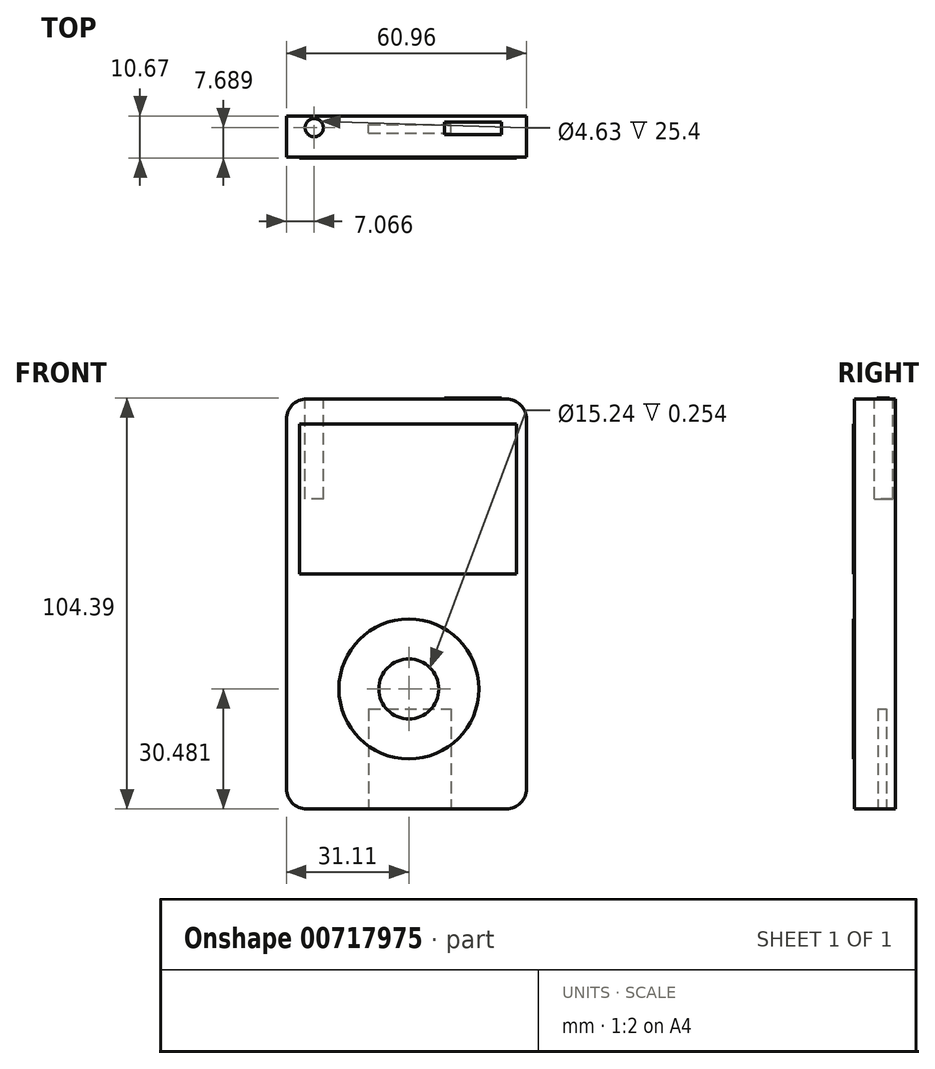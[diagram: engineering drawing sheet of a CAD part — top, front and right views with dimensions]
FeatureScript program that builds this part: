
annotation { "Feature Type Name" : "Feature", "Feature Type Description" : "" }
export const myFeature = defineFeature(function(context is Context, id is Id, definition is map)
    precondition{}
    {
        {
            var Q0;
            Q0=qCreatedBy(makeId("Front.planeOp"),FACE);
            var sketch = newSketch(context, id + "F0", { "sketchPlane" : qUnion([Q0])});
            skLineSegment(sketch, "E0.bottom", {"start": v(22.89, -46.83) * mm, "end": v(-38.07, -46.83) * mm});
            skLineSegment(sketch, "E0.top", {"start": v(22.89, 57.31) * mm, "end": v(-38.07, 57.31) * mm});
            skLineSegment(sketch, "E0.left", {"start": v(22.89, -46.83) * mm, "end": v(22.89, 57.31) * mm});
            skLineSegment(sketch, "E0.right", {"start": v(-38.07, -46.83) * mm, "end": v(-38.07, 57.31) * mm});
            skSolve(sketch);
        }
        {
            var Q0;
            Q0 = qSketchRegion(id + "F0", true);
            extrude(context, id + "F1", {"entities" : qUnion([Q0]), "depth" : 10.4 * mm, "offsetDistance" : 25.4 * mm});
        }
        {
            var Q0;
            Q0=makeQuery(id+"F1.opExtrude","CAP_FACE",FACE,{"disambiguationData":[OSD([sQuery(id+"F0.wireOp",EDGE,"E0.bottom"),sQuery(id+"F0.wireOp",EDGE,"E0.top"),sQuery(id+"F0.wireOp",EDGE,"E0.left"),sQuery(id+"F0.wireOp",EDGE,"E0.right")])],"isStart":false});
            var sketch = newSketch(context, id + "F2", { "sketchPlane" : qUnion([Q0])});
            skLineSegment(sketch, "E1.bottom", {"start": v(-34.8, 50.96) * mm, "end": v(20.39, 50.96) * mm});
            skLineSegment(sketch, "E1.top", {"start": v(-34.8, 12.86) * mm, "end": v(20.39, 12.86) * mm});
            skLineSegment(sketch, "E1.left", {"start": v(-34.8, 50.96) * mm, "end": v(-34.8, 12.86) * mm});
            skLineSegment(sketch, "E1.right", {"start": v(20.39, 50.96) * mm, "end": v(20.39, 12.86) * mm});
            skLineSegment(sketch, "E2", {"start": v(-38.07, 57.31) * mm, "end": v(-38.07, 31.91) * mm});
            skPoint(sketch, "E2.endSnap0", {"position": v(-34.8, 31.91) * mm});
            skSolve(sketch);
        }
        {
            var Q0;
            Q0=makeQuery(id+"F2.imprint","IMPRINT",FACE,{"disambiguationData":[TD([[makeQuery(id+"F2.imprint","IMPRINT",EDGE,{"derivedFrom":sQuery(id+"F2.wireOp",EDGE,"E1.bottom")}),1.0]])]});
            var sketch = newSketch(context, id + "F3", { "sketchPlane" : qUnion([Q0])});
            skCircle(sketch, "E3", {"center": v(-6.96, -16.35) * mm, "radius": 17.78 * mm});
            skCircle(sketch, "E4", {"center": v(-6.96, -16.35) * mm, "radius": 7.62 * mm});
            skSolve(sketch);
        }
        {
            var Q0;
            Q0 = qSketchRegion(id + "F3", true);
            extrude(context, id + "F4", {"entities" : qUnion([Q0]), "operationType" : NewBodyOperationType.ADD, "depth" : 0.25 * mm, "offsetDistance" : 25.4 * mm});
        }
        {
            var Q0;
            Q0 = qSketchRegion(id + "F2", true);
            extrude(context, id + "F5", {"entities" : qUnion([Q0]), "operationType" : NewBodyOperationType.ADD, "depth" : 0.25 * mm, "offsetDistance" : 25.4 * mm});
        }
        {
            var Q0;
            Q0=makeQuery(id+"F1.opExtrude","SWEPT_FACE",FACE,{"disambiguationData":[OSD([sQuery(id+"F0.wireOp",EDGE,"E0.top")])]});
            var sketch = newSketch(context, id + "F6", { "sketchPlane" : qUnion([Q0])});
            skCircle(sketch, "E5", {"center": v(-31, -2.98) * mm, "radius": 2.32 * mm});
            skSolve(sketch);
        }
        {
            var Q0;
            Q0 = qSketchRegion(id + "F6", true);
            extrude(context, id + "F7", {"entities" : qUnion([Q0]), "operationType" : NewBodyOperationType.REMOVE, "oppositeDirection" : true, "depth" : 25.4 * mm, "offsetDistance" : 25.4 * mm});
        }
        {
            var Q0;
            Q0=makeQuery(id+"F1.opExtrude","SWEPT_FACE",FACE,{"disambiguationData":[OSD([sQuery(id+"F0.wireOp",EDGE,"E0.top")])]});
            var sketch = newSketch(context, id + "F8", { "sketchPlane" : qUnion([Q0])});
            skLineSegment(sketch, "E6.bottom", {"start": v(2.13, -1.5) * mm, "end": v(16.53, -1.5) * mm});
            skLineSegment(sketch, "E6.top", {"start": v(2.13, -4.68) * mm, "end": v(16.53, -4.68) * mm});
            skLineSegment(sketch, "E6.left", {"start": v(2.13, -1.5) * mm, "end": v(2.13, -4.68) * mm});
            skLineSegment(sketch, "E6.right", {"start": v(16.53, -1.5) * mm, "end": v(16.53, -4.68) * mm});
            skSolve(sketch);
        }
        {
            var Q0;
            Q0 = qSketchRegion(id + "F8", true);
            extrude(context, id + "F9", {"entities" : qUnion([Q0]), "operationType" : NewBodyOperationType.ADD, "depth" : 0.25 * mm, "offsetDistance" : 25.4 * mm});
        }
        {
            var Q0;
            Q0=makeQuery(id+"F1.opExtrude","SWEPT_FACE",FACE,{"disambiguationData":[OSD([sQuery(id+"F0.wireOp",EDGE,"E0.bottom")])]});
            var sketch = newSketch(context, id + "F10", { "sketchPlane" : qUnion([Q0])});
            skLineSegment(sketch, "E7.bottom", {"start": v(-17.18, 4.38) * mm, "end": v(3.7, 4.38) * mm});
            skLineSegment(sketch, "E7.top", {"start": v(-17.18, 2.24) * mm, "end": v(3.7, 2.24) * mm});
            skLineSegment(sketch, "E7.left", {"start": v(-17.18, 4.38) * mm, "end": v(-17.18, 2.24) * mm});
            skLineSegment(sketch, "E7.right", {"start": v(3.7, 4.38) * mm, "end": v(3.7, 2.24) * mm});
            skSolve(sketch);
        }
        {
            var Q0;
            Q0 = qSketchRegion(id + "F10", true);
            extrude(context, id + "F11", {"entities" : qUnion([Q0]), "operationType" : NewBodyOperationType.REMOVE, "oppositeDirection" : true, "depth" : 25.4 * mm, "offsetDistance" : 25.4 * mm});
        }
        {
            var Q0;
            Q0=makeQuery(id+"F1.opExtrude","SWEPT_EDGE",EDGE,{"disambiguationData":[OSD([sQuery(id+"F0.wireOp",EDGE,"E0.bottom"),sQuery(id+"F0.wireOp",EDGE,"E0.right")])]});
            fillet(context, id + "F12", {"entities" : qUnion([Q0]), "radius" : 5.08 * mm, "tangentPropagation" : true, "allowEdgeOverflow" : false});
        }
        {
            var Q0;
            Q0=makeQuery(id+"F1.opExtrude","SWEPT_EDGE",EDGE,{"disambiguationData":[OSD([sQuery(id+"F0.wireOp",EDGE,"E0.top"),sQuery(id+"F0.wireOp",EDGE,"E0.right")])]});
            fillet(context, id + "F13", {"entities" : qUnion([Q0]), "radius" : 5.08 * mm, "tangentPropagation" : true, "allowEdgeOverflow" : false});
        }
        {
            var Q0;
            Q0=makeQuery(id+"F1.opExtrude","SWEPT_EDGE",EDGE,{"disambiguationData":[OSD([sQuery(id+"F0.wireOp",EDGE,"E0.bottom"),sQuery(id+"F0.wireOp",EDGE,"E0.left")])]});
            fillet(context, id + "F14", {"entities" : qUnion([Q0]), "radius" : 5.08 * mm, "tangentPropagation" : true, "allowEdgeOverflow" : false});
        }
        {
            var Q0;
            Q0=makeQuery(id+"F1.opExtrude","SWEPT_EDGE",EDGE,{"disambiguationData":[OSD([sQuery(id+"F0.wireOp",EDGE,"E0.top"),sQuery(id+"F0.wireOp",EDGE,"E0.left")])]});
            fillet(context, id + "F15", {"entities" : qUnion([Q0]), "radius" : 5.08 * mm, "tangentPropagation" : true, "allowEdgeOverflow" : false});
        }
    });
